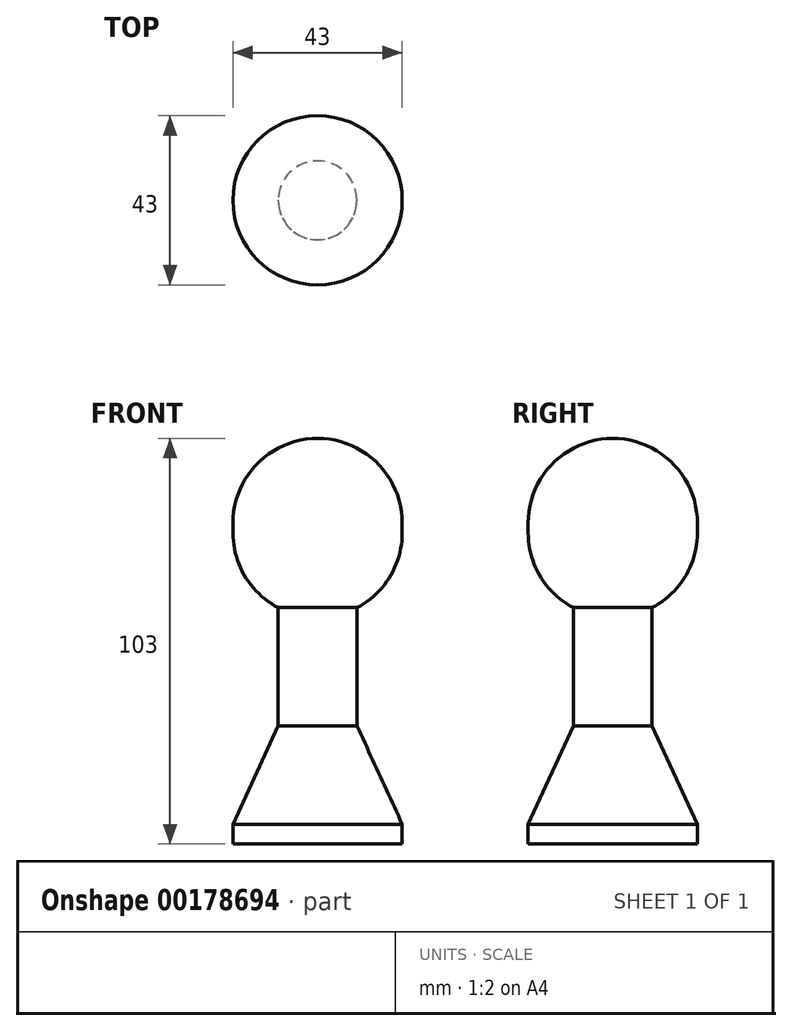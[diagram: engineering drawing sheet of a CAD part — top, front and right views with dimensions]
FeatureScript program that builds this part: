
annotation { "Feature Type Name" : "Feature", "Feature Type Description" : "" }
export const myFeature = defineFeature(function(context is Context, id is Id, definition is map)
    precondition{}
    {
        {
            var Q0;
            Q0=qCreatedBy(makeId("Top.planeOp"),FACE);
            var sketch = newSketch(context, id + "F0", { "sketchPlane" : qUnion([Q0])});
            skCircle(sketch, "E0", {"center": v(0, 0) * mm, "radius": 21.5 * mm});
            skSolve(sketch);
        }
        {
            var Q0;
            Q0=makeQuery(id+"F0.imprint","IMPRINT",FACE,{"disambiguationData":[TD([[makeQuery(id+"F0.imprint","IMPRINT",EDGE,{"derivedFrom":sQuery(id+"F0.wireOp",EDGE,"E0")}),1.0]])]});
            extrude(context, id + "F1", {"entities" : qUnion([Q0]), "depth" : 30 * mm});
        }
        {
            var Q0;
            Q0=makeQuery(id+"F1.opExtrude","CAP_EDGE",EDGE,{"disambiguationData":[OSD([sQuery(id+"F0.wireOp",EDGE,"E0")])],"isStart":false});
            chamfer(context, id + "F2", {"entities" : qUnion([Q0]), "chamferType" : ChamferType.TWO_OFFSETS, "width1" : ((43 / 2) - 10) * mm, "oppositeDirection" : false, "width2" : 25 * mm, "tangentPropagation" : true});
        }
        {
            var Q0;
            Q0=makeQuery(id+"F1.opExtrude","CAP_FACE",FACE,{"disambiguationData":[OSD([sQuery(id+"F0.wireOp",EDGE,"E0")])],"isStart":false});
            extrude(context, id + "F3", {"entities" : qUnion([Q0]), "operationType" : NewBodyOperationType.ADD, "depth" : 30 * mm});
        }
        {
            var Q0;
            Q0=makeQuery(id+"F3.opExtrude","CAP_FACE",FACE,{"disambiguationData":[OSD([sQuery(id+"F0.wireOp",EDGE,"E0")])],"isStart":false});
            var sketch = newSketch(context, id + "F4", { "sketchPlane" : qUnion([Q0])});
            skCircle(sketch, "E1", {"center": v(0, 0) * mm, "radius": 21.5 * mm});
            skSolve(sketch);
        }
        {
            var Q0;
            Q0=qSketchRegion(id+"F4",true);
            extrude(context, id + "F5", {"entities" : qUnion([Q0]), "operationType" : NewBodyOperationType.ADD, "depth" : 43 * mm});
        }
        {
            var Q0;
            Q0=makeQuery(id+"F5.opExtrude","CAP_EDGE",EDGE,{"disambiguationData":[OSD([sQuery(id+"F4.wireOp",EDGE,"E1")])],"isStart":false});
            var Q1;
            Q1=makeQuery(id+"F5.opExtrude","CAP_EDGE",EDGE,{"disambiguationData":[OSD([sQuery(id+"F4.wireOp",EDGE,"E1")])],"isStart":true});
            fillet(context, id + "F6", {"entities" : qUnion([Q0, Q1]), "radius" : ((43 / 2) - 0) * mm, "tangentPropagation" : true, "allowEdgeOverflow" : false});
        }
    });
